# Revit family: Haworth_JiveTable_RectangleSwivelBase
name_source: partatom
category: Furniture Systems
revit_build: Autodesk Revit 2018 (Build: 20170223_1515(x64)
units: mm (PartAtom-declared; Revit-internal decimal feet)

## family parameters
Always vertical = Yes
Cut with Voids When Loaded = No
OmniClass Number = 23.40.70.14.64.21
OmniClass Title = Systems Furniture
Part Type = Normal
Room Calculation Point = No
Round Connector Dimension = Use Diameter
Shared = No
Work Plane-Based = No

## types (52) — shared parameters
Actual Height = 29"
Assembly Code = E2020200
Custom Size = No
Leg Finish = Haworth _ Paint _ Graphite
Leg Height = 27 13/16"
Manufacturer = Haworth, Inc.
Max. Depth = 48"
Max. Height = 29"
Max. Width = 72"
Min. Depth = 18"
Min. Height = 29"
Min. Width = 24"
Model = Haworth Jive
Revision Number = 0
Size = Verify Final Dim. w/ Haworth
Standard Depths = 18, 24, 30, 36, 42, 48 in.
Standard Widths = 24, 30, 36, 42, 48, 54, 60, 66, 72 in.
Table Edge Finish = Haworth _ Laminate _ Putty H-AA
Table Finish = Haworth _ Laminate _ Putty H-AA
Table Thickness = 1 3/16"
URL = http://www.haworth.com
URL - Product = https://www.haworth.com
Warranty = http://haworth.com

## per-type parameters (varying)
| type | Actual Depth | Actual Width | Casters | Depth | Description | Glides | Width |
| 18d 48w - With Casters | 18" | 48" | Yes | 18" | Haworth Swivel Table Rectangle - 18d 48w - With Casters | No | 48" |
| 18d 54w - With Casters | 18" | 54" | Yes | 18" | Haworth Swivel Table Rectangle - 18d 54w - With Casters | No | 54" |
| 18d 60w - With Casters | 18" | 60" | Yes | 18" | Haworth Swivel Table Rectangle - 18d 60w - With Casters | No | 60" |
| 18d 66w - With Casters | 18" | 66" | Yes | 18" | Haworth Swivel Table Rectangle - 18d 66w - With Casters | No | 66" |
| 18d 72w - With Casters | 18" | 72" | Yes | 18" | Haworth Swivel Table Rectangle - 18d 72w - With Casters | No | 72" |
| 18d 48w - With Glides | 18" | 48" | No | 18" | Haworth Swivel Table Rectangle - 18d 48w - With Glides | Yes | 48" |
| 18d 54w - With Glides | 18" | 54" | No | 18" | Haworth Swivel Table Rectangle - 18d 54w - With Glides | Yes | 54" |
| 18d 60w - With Glides | 18" | 60" | No | 18" | Haworth Swivel Table Rectangle - 18d 60w - With Glides | Yes | 60" |
| 18d 66w - With Glides | 18" | 66" | No | 18" | Haworth Swivel Table Rectangle - 18d 66w - With Glides | Yes | 66" |
| 18d 72w - With Glides | 18" | 72" | No | 18" | Haworth Swivel Table Rectangle - 18d 72w - With Glides | Yes | 72" |
| 24d 36w - With Casters | 24" | 36" | Yes | 24" | Haworth Swivel Table Rectangle - 24d 36w - With Casters | No | 36" |
| 24d 42w - With Casters | 24" | 42" | Yes | 24" | Haworth Swivel Table Rectangle - 24d 42w - With Casters | No | 42" |
| 24d 48w - With Casters | 24" | 48" | Yes | 24" | Haworth Swivel Table Rectangle - 24d 48w - With Casters | No | 48" |
| 24d 54w - With Casters | 24" | 54" | Yes | 24" | Haworth Swivel Table Rectangle - 24d 54w - With Casters | No | 54" |
| 24d 60w - With Casters | 24" | 60" | Yes | 24" | Haworth Swivel Table Rectangle - 24d 60w - With Casters | No | 60" |
| 24d 66w - With Casters | 24" | 66" | Yes | 24" | Haworth Swivel Table Rectangle - 24d 66w - With Casters | No | 66" |
| 24d 72w - With Casters | 24" | 72" | Yes | 24" | Haworth Swivel Table Rectangle - 24d 72w - With Casters | No | 72" |
| 24d 36w - With Glides | 24" | 36" | No | 24" | Haworth Swivel Table Rectangle - 24d 36w - With Glides | Yes | 36" |
| 24d 42w - With Glides | 24" | 42" | No | 24" | Haworth Swivel Table Rectangle - 24d 42w - With Glides | Yes | 42" |
| 24d 48w - With Glides | 24" | 48" | No | 24" | Haworth Swivel Table Rectangle - 24d 48w - With Glides | Yes | 48" |
| 24d 54w - With Glides | 24" | 54" | No | 24" | Haworth Swivel Table Rectangle - 24d 54w - With Glides | Yes | 54" |
| 24d 60w - With Glides | 24" | 60" | No | 24" | Haworth Swivel Table Rectangle - 24d 60w - With Glides | Yes | 60" |
| 24d 66w - With Glides | 24" | 66" | No | 24" | Haworth Swivel Table Rectangle - 24d 66w - With Glides | Yes | 66" |
| 24d 72w - With Glides | 24" | 72" | No | 24" | Haworth Swivel Table Rectangle - 24d 72w - With Glides | Yes | 72" |
| 30d 36w - With Casters | 30" | 36" | Yes | 30" | Haworth Swivel Table Rectangle - 30d 36w - With Casters | No | 36" |
| 30d 42w - With Casters | 30" | 42" | Yes | 30" | Haworth Swivel Table Rectangle - 30d 42w - With Casters | No | 42" |
| 30d 48w - With Casters | 30" | 48" | Yes | 30" | Haworth Swivel Table Rectangle - 30d 48w - With Casters | No | 48" |
| 30d 54w - With Casters | 30" | 54" | Yes | 30" | Haworth Swivel Table Rectangle - 30d 54w - With Casters | No | 54" |
| 30d 60w - With Casters | 30" | 60" | Yes | 30" | Haworth Swivel Table Rectangle - 30d 60w - With Casters | No | 60" |
| 30d 66w - With Casters | 30" | 66" | Yes | 30" | Haworth Swivel Table Rectangle - 30d 66w - With Casters | No | 66" |
| 30d 72w - With Casters | 30" | 72" | Yes | 30" | Haworth Swivel Table Rectangle - 30d 72w - With Casters | No | 72" |
| 30d 36w - With Glides | 30" | 36" | No | 30" | Haworth Swivel Table Rectangle - 30d 36w - With Glides | Yes | 36" |
| 30d 42w - With Glides | 30" | 42" | No | 30" | Haworth Swivel Table Rectangle - 30d 42w - With Glides | Yes | 42" |
| 30d 48w - With Glides | 30" | 48" | No | 30" | Haworth Swivel Table Rectangle - 30d 48w - With Glides | Yes | 48" |
| 30d 54w - With Glides | 30" | 54" | No | 30" | Haworth Swivel Table Rectangle - 30d 54w - With Glides | Yes | 54" |
| 30d 60w - With Glides | 30" | 60" | No | 30" | Haworth Swivel Table Rectangle - 30d 60w - With Glides | Yes | 60" |
| 30d 66w - With Glides | 30" | 66" | No | 30" | Haworth Swivel Table Rectangle - 30d 66w - With Glides | Yes | 66" |
| 30d 72w - With Glides | 30" | 72" | No | 30" | Haworth Swivel Table Rectangle - 30d 72w - With Glides | Yes | 72" |
| 36d 66w - With Casters | 36" | 66" | Yes | 36" | Haworth Swivel Table Rectangle - 36d 66w - With Casters | No | 66" |
| 36d 72w - With Casters | 36" | 72" | Yes | 36" | Haworth Swivel Table Rectangle - 36d 72w - With Casters | No | 72" |
| 36d 66w - With Glides | 36" | 66" | No | 36" | Haworth Swivel Table Rectangle - 36d 66w - With Glides | Yes | 66" |
| 36d 72w - With Glides | 36" | 72" | No | 36" | Haworth Swivel Table Rectangle - 36d 72w - With Glides | Yes | 72" |
| 24d 24w - With Casters | 24" | 24" | Yes | 24" | Haworth Swivel Table Rectangle - 24d 24w - With Casters | No | 24" |
| 30d 30w - With Casters | 30" | 30" | Yes | 30" | Haworth Swivel Table Rectangle - 30d 30w - With Casters | No | 30" |
| 36d 36w - With Casters | 36" | 36" | Yes | 36" | Haworth Swivel Table Rectangle - 36d 36w - With Casters | No | 36" |
| 42d 42w - With Casters | 42" | 42" | Yes | 42" | Haworth Swivel Table Rectangle - 42d 42w - With Casters | No | 42" |
| 48d 48w - With Casters | 48" | 48" | Yes | 48" | Haworth Swivel Table Rectangle - 48d 48w - With Casters | No | 48" |
| 24d 24w - With Glides | 24" | 24" | No | 24" | Haworth Swivel Table Rectangle - 24d 24w - With Glides | Yes | 24" |
| 30d 30w - With Glides | 30" | 30" | No | 30" | Haworth Swivel Table Rectangle - 30d 30w - With Glides | Yes | 30" |
| 36d 36w - With Glides | 36" | 36" | No | 36" | Haworth Swivel Table Rectangle - 36d 36w - With Glides | Yes | 36" |
| 42d 42w - With Glides | 42" | 42" | No | 42" | Haworth Swivel Table Rectangle - 42d 42w - With Glides | Yes | 42" |
| 48d 48w - With Glides | 48" | 48" | No | 48" | Haworth Swivel Table Rectangle - 48d 48w - With Glides | Yes | 48" |

## geometry (parser evidence)
native form markers: Sweep x6
no freeform markers — native parametric forms only
